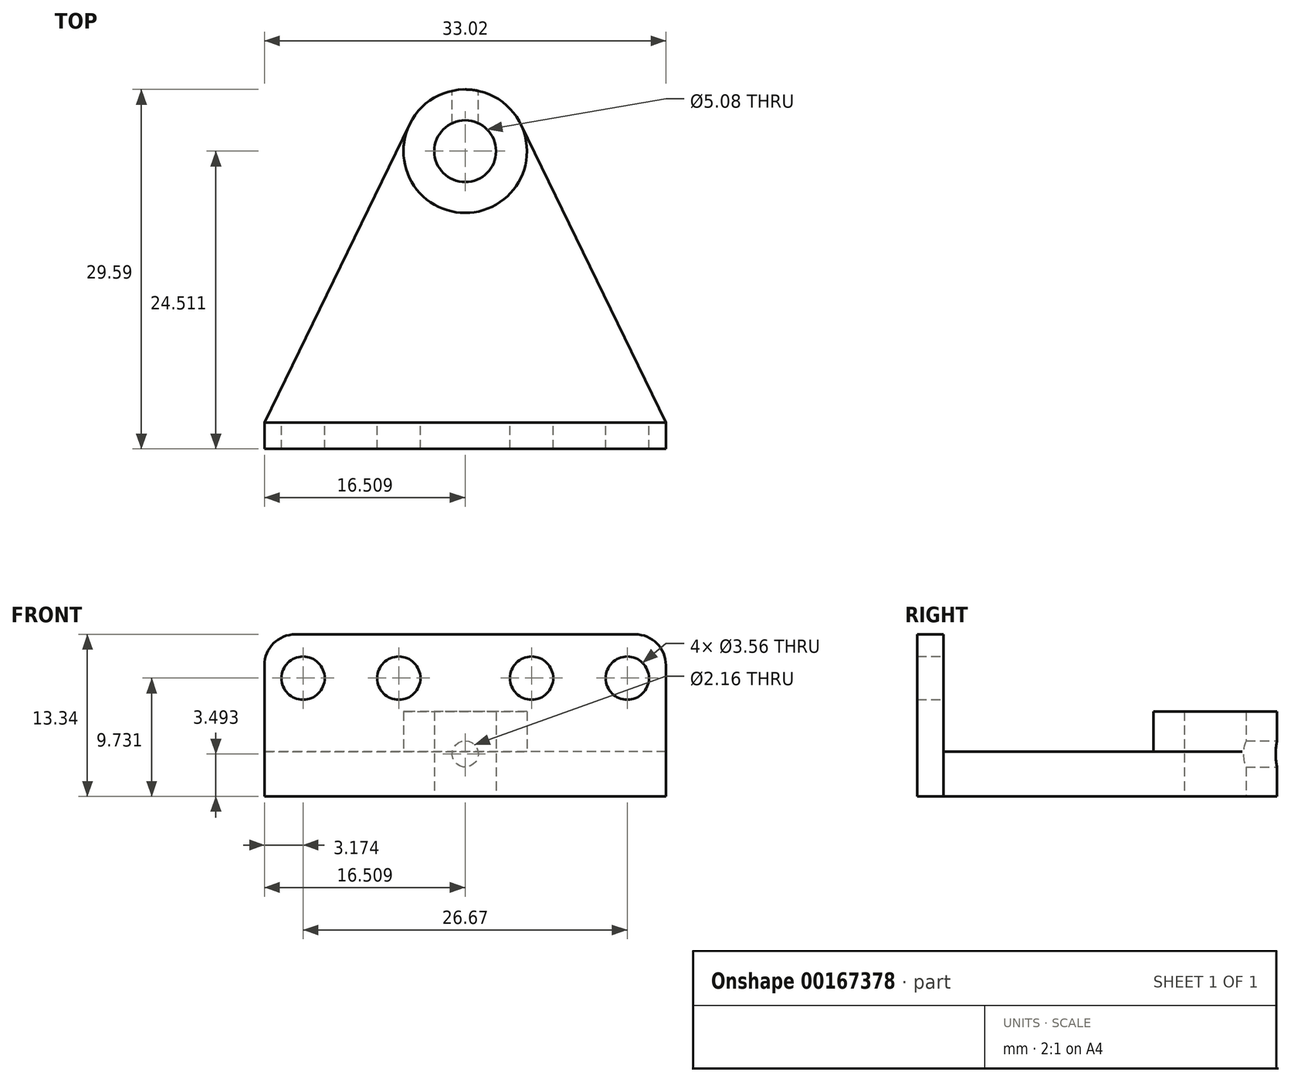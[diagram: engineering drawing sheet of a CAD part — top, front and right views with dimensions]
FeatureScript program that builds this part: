
annotation { "Feature Type Name" : "Feature", "Feature Type Description" : "" }
export const myFeature = defineFeature(function(context is Context, id is Id, definition is map)
    precondition{}
    {
        {
            var Q0;
            Q0=qCreatedBy(makeId("Top.planeOp"),FACE);
            var sketch = newSketch(context, id + "F0", { "sketchPlane" : qUnion([Q0])});
            skLineSegment(sketch, "E0.bottom", {"start": v(-4, 0) * mm, "end": v(29.03, 0) * mm});
            skLineSegment(sketch, "E0.top", {"start": v(-4, 2.16) * mm, "end": v(29.03, 2.16) * mm});
            skLineSegment(sketch, "E0.left", {"start": v(-4, 0) * mm, "end": v(-4, 2.16) * mm});
            skLineSegment(sketch, "E0.right", {"start": v(29.03, 0) * mm, "end": v(29.03, 2.16) * mm});
            skCircle(sketch, "E1", {"center": v(12.52, 24.51) * mm, "radius": 2.54 * mm});
            skPoint(sketch, "E1.centerSnap0", {"position": v(12.52, 2.16) * mm});
            skCircle(sketch, "E2", {"center": v(12.52, 24.51) * mm, "radius": 5.08 * mm});
            skLineSegment(sketch, "E3", {"start": v(-4, 2.16) * mm, "end": v(7.95, 26.73) * mm});
            skLineSegment(sketch, "E4", {"start": v(29.03, 2.16) * mm, "end": v(17.09, 26.73) * mm});
            skSolve(sketch);
        }
        {
            var Q0;
            Q0=makeQuery(id+"F0.imprint","IMPRINT",FACE,{"disambiguationData":[TD([[makeQuery(id+"F0.imprint","IMPRINT",EDGE,{"derivedFrom":sQuery(id+"F0.wireOp",EDGE,"E0.bottom")}),1.0]])]});
            var Q1;
            Q1=makeQuery(id+"F0.imprint","IMPRINT",FACE,{"disambiguationData":[TD([[makeQuery(id+"F0.imprint","IMPRINT",EDGE,{"derivedFrom":sQuery(id+"F0.wireOp",EDGE,"E0.top")}),1.0]])]});
            var Q2;
            Q2=makeQuery(id+"F0.imprint","IMPRINT",FACE,{"disambiguationData":[TD([[makeQuery(id+"F0.imprint","IMPRINT",EDGE,{"derivedFrom":sQuery(id+"F0.wireOp",EDGE,"E1")}),-1.0]])]});
            extrude(context, id + "F1", {"entities" : qUnion([Q0, Q1, Q2]), "depth" : 3.68 * mm});
        }
        {
            var Q0;
            Q0=makeQuery(id+"F0.imprint","IMPRINT",FACE,{"disambiguationData":[TD([[makeQuery(id+"F0.imprint","IMPRINT",EDGE,{"derivedFrom":sQuery(id+"F0.wireOp",EDGE,"E0.bottom")}),1.0]])]});
            extrude(context, id + "F2", {"entities" : qUnion([Q0]), "operationType" : NewBodyOperationType.ADD, "depth" : 13.33 * mm});
        }
        {
            var Q0;
            Q0=makeQuery(id+"F0.imprint","IMPRINT",FACE,{"disambiguationData":[TD([[makeQuery(id+"F0.imprint","IMPRINT",EDGE,{"derivedFrom":sQuery(id+"F0.wireOp",EDGE,"E1")}),-1.0]])]});
            extrude(context, id + "F3", {"entities" : qUnion([Q0]), "operationType" : NewBodyOperationType.ADD, "depth" : 7 * mm});
        }
        {
            var Q0;
            Q0=makeQuery(id+"F2.opExtrude","SWEPT_FACE",FACE,{"disambiguationData":[OSD([sQuery(id+"F0.wireOp",EDGE,"E0.top")])]});
            var sketch = newSketch(context, id + "F4", { "sketchPlane" : qUnion([Q0])});
            skCircle(sketch, "E5", {"center": v(0.82, 9.73) * mm, "radius": 1.78 * mm});
            skCircle(sketch, "E6", {"center": v(-25.85, 9.73) * mm, "radius": 1.78 * mm});
            skCircle(sketch, "E7", {"center": v(-17.98, 9.73) * mm, "radius": 1.78 * mm});
            skCircle(sketch, "E8", {"center": v(-7.06, 9.73) * mm, "radius": 1.78 * mm});
            skSolve(sketch);
        }
        {
            var Q0;
            Q0 = qSketchRegion(id + "F4", true);
            extrude(context, id + "F5", {"entities" : qUnion([Q0]), "operationType" : NewBodyOperationType.REMOVE, "oppositeDirection" : true, "depth" : 25.4 * mm});
        }
        {
            var Q0;
            Q0=makeQuery(id+"F2.opExtrude","CAP_EDGE",EDGE,{"disambiguationData":[OSD([sQuery(id+"F0.wireOp",EDGE,"E0.left")])],"isStart":false});
            var Q1;
            Q1=makeQuery(id+"F2.opExtrude","CAP_EDGE",EDGE,{"disambiguationData":[OSD([sQuery(id+"F0.wireOp",EDGE,"E0.right")])],"isStart":false});
            fillet(context, id + "F6", {"entities" : qUnion([Q0, Q1]), "radius" : 2.54 * mm, "tangentPropagation" : true, "allowEdgeOverflow" : false});
        }
        {
            var Q0;
            Q0=qCreatedBy(makeId("Front.planeOp"),FACE);
            cPlane(context, id + "F7", {"entities" : qUnion([Q0]), "cplaneType" : CPlaneType.OFFSET, "offset" : 29.6 * mm, "oppositeDirection" : true, "width" : 152.4 * mm, "height" : 152.4 * mm});
        }
        {
            var Q0;
            Q0=qCreatedBy(id+"F7.planeOp",FACE);
            var sketch = newSketch(context, id + "F8", { "sketchPlane" : qUnion([Q0])});
            skLineSegment(sketch, "E9.0", {"start": v(17.09, 0) * mm, "end": v(7.95, 0) * mm});
            skPoint(sketch, "E10", {"position": v(12.52, 0) * mm});
            skCircle(sketch, "E11", {"center": v(12.52, 3.5) * mm, "radius": 1.08 * mm});
            skSolve(sketch);
        }
        {
            var Q0;
            Q0 = qSketchRegion(id + "F8", true);
            extrude(context, id + "F9", {"entities" : qUnion([Q0]), "operationType" : NewBodyOperationType.REMOVE, "depth" : 3.8 * mm});
        }
    });
